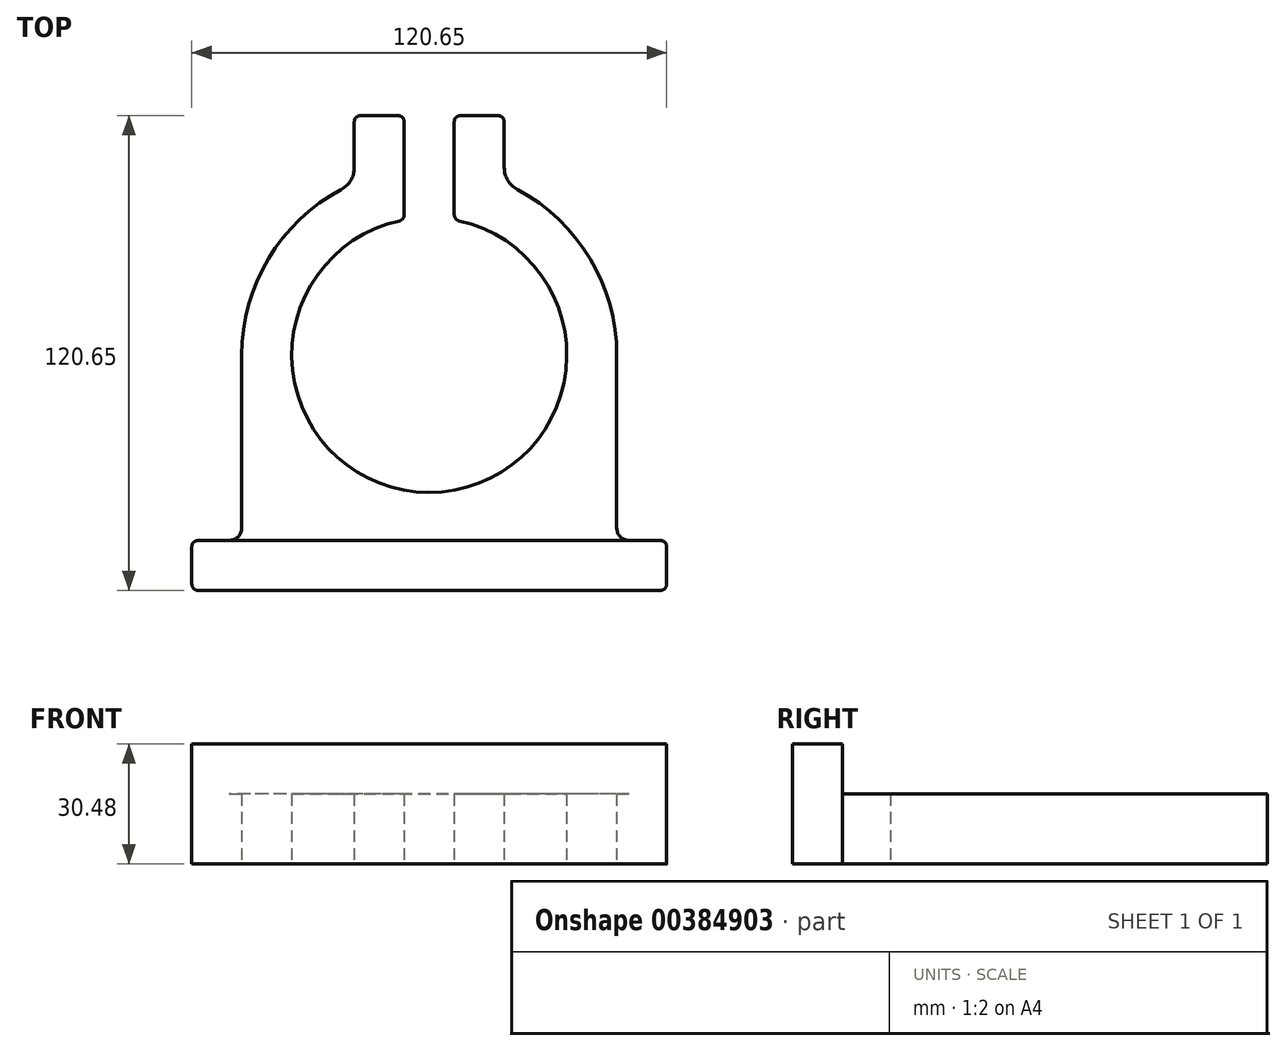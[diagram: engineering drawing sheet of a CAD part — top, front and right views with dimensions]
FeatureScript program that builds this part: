
annotation { "Feature Type Name" : "Feature", "Feature Type Description" : "" }
export const myFeature = defineFeature(function(context is Context, id is Id, definition is map)
    precondition{}
    {
        {
            var Q0;
            Q0=qCreatedBy(makeId("Top.planeOp"),FACE);
            var sketch = newSketch(context, id + "F0", { "sketchPlane" : qUnion([Q0])});
            skLineSegment(sketch, "E0", {"start": v(1.59, 0) * mm, "end": v(119.06, 0) * mm});
            skLineSegment(sketch, "E1", {"start": v(120.65, 1.59) * mm, "end": v(120.65, 11.11) * mm});
            skLineSegment(sketch, "E2", {"start": v(119.06, 12.7) * mm, "end": v(111.13, 12.7) * mm});
            skLineSegment(sketch, "E3", {"start": v(107.95, 15.88) * mm, "end": v(107.95, 59.82) * mm});
            skLineSegment(sketch, "E4", {"start": v(12.7, 59.82) * mm, "end": v(12.7, 15.88) * mm});
            skLineSegment(sketch, "E5", {"start": v(9.52, 12.7) * mm, "end": v(1.59, 12.7) * mm});
            skLineSegment(sketch, "E6", {"start": v(0, 11.11) * mm, "end": v(0, 1.59) * mm});
            skArc(sketch, "E7", {"start": v(107.95, 59.82) * mm, "mid": v(101.16, 84.32) * mm, "end": v(82.74, 101.84) * mm});
            skPoint(sketch, "E7.startSnap0", {"position": v(60.33, 59.82) * mm});
            skLineSegment(sketch, "E8.trimOffspring", {"start": v(107.95, 59.82) * mm, "end": v(107.95, 59.82) * mm});
            skPoint(sketch, "E9.orphan", {"position": v(60.33, 107.44) * mm});
            skArc(sketch, "E10", {"start": v(52.73, 93.9) * mm, "mid": v(60.33, 24.9) * mm, "end": v(67.92, 93.9) * mm});
            skLineSegment(sketch, "E11", {"start": v(53.98, 95.46) * mm, "end": v(53.98, 119.06) * mm});
            skLineSegment(sketch, "E12", {"start": v(52.39, 120.65) * mm, "end": v(42.86, 120.65) * mm});
            skLineSegment(sketch, "E13", {"start": v(41.28, 119.06) * mm, "end": v(41.28, 107.44) * mm});
            skLineSegment(sketch, "E14", {"start": v(60.33, 59.82) * mm, "end": v(60.33, 128.19) * mm, "construction": true});
            skLineSegment(sketch, "E15.MirrorCS", {"start": v(66.67, 95.46) * mm, "end": v(66.67, 119.06) * mm});
            skLineSegment(sketch, "E16.MirrorCS", {"start": v(68.26, 120.65) * mm, "end": v(77.79, 120.65) * mm});
            skLineSegment(sketch, "E17.MirrorCS", {"start": v(79.38, 119.06) * mm, "end": v(79.38, 107.44) * mm});
            skArc(sketch, "E18.trimOffspring", {"start": v(37.91, 101.84) * mm, "mid": v(19.49, 84.32) * mm, "end": v(12.7, 59.82) * mm});
            skLineSegment(sketch, "E19", {"start": v(60.33, 0) * mm, "end": v(60.33, 37.1) * mm, "construction": true});
            skPoint(sketch, "E20.visualSharp", {"position": v(41.28, 103.47) * mm});
            skArc(sketch, "E20.filletArc", {"start": v(37.91, 101.84) * mm, "mid": v(40.37, 104.17) * mm, "end": v(41.28, 107.44) * mm});
            skPoint(sketch, "E21.visualSharp", {"position": v(79.38, 103.47) * mm});
            skArc(sketch, "E21.filletArc", {"start": v(79.38, 107.44) * mm, "mid": v(80.28, 104.17) * mm, "end": v(82.74, 101.84) * mm});
            skPoint(sketch, "E22.visualSharp", {"position": v(107.95, 12.7) * mm});
            skPoint(sketch, "E23.visualSharp", {"position": v(12.7, 12.7) * mm});
            skArc(sketch, "E24.filletArc", {"start": v(52.73, 93.9) * mm, "mid": v(53.63, 94.46) * mm, "end": v(53.98, 95.46) * mm});
            skPoint(sketch, "E25.visualSharp", {"position": v(120.65, 12.7) * mm});
            skArc(sketch, "E25.filletArc", {"start": v(120.65, 11.11) * mm, "mid": v(120.19, 12.24) * mm, "end": v(119.06, 12.7) * mm});
            skPoint(sketch, "E26.visualSharp", {"position": v(120.65, 0) * mm});
            skArc(sketch, "E26.filletArc", {"start": v(119.06, 0) * mm, "mid": v(120.19, 0.46) * mm, "end": v(120.65, 1.59) * mm});
            skPoint(sketch, "E27.visualSharp", {"position": v(0, 0) * mm});
            skArc(sketch, "E27.filletArc", {"start": v(0, 1.59) * mm, "mid": v(0.46, 0.46) * mm, "end": v(1.59, 0) * mm});
            skPoint(sketch, "E28.visualSharp", {"position": v(0, 12.7) * mm});
            skArc(sketch, "E28.filletArc", {"start": v(1.59, 12.7) * mm, "mid": v(0.46, 12.24) * mm, "end": v(0, 11.11) * mm});
            skPoint(sketch, "E29.visualSharp", {"position": v(66.67, 94.16) * mm});
            skArc(sketch, "E29.filletArc", {"start": v(66.67, 95.46) * mm, "mid": v(67.02, 94.46) * mm, "end": v(67.92, 93.9) * mm});
            skPoint(sketch, "E30.visualSharp", {"position": v(41.28, 120.65) * mm});
            skArc(sketch, "E30.filletArc", {"start": v(42.86, 120.65) * mm, "mid": v(41.74, 120.19) * mm, "end": v(41.28, 119.06) * mm});
            skPoint(sketch, "E31.visualSharp", {"position": v(53.98, 120.65) * mm});
            skArc(sketch, "E31.filletArc", {"start": v(53.98, 119.06) * mm, "mid": v(53.51, 120.19) * mm, "end": v(52.39, 120.65) * mm});
            skPoint(sketch, "E32.visualSharp", {"position": v(79.38, 120.65) * mm});
            skArc(sketch, "E32.filletArc", {"start": v(79.38, 119.06) * mm, "mid": v(78.91, 120.19) * mm, "end": v(77.79, 120.65) * mm});
            skPoint(sketch, "E33.visualSharp", {"position": v(66.67, 120.65) * mm});
            skArc(sketch, "E33.filletArc", {"start": v(68.26, 120.65) * mm, "mid": v(67.14, 120.19) * mm, "end": v(66.67, 119.06) * mm});
            skArc(sketch, "E34.filletArc", {"start": v(9.52, 12.7) * mm, "mid": v(11.77, 13.63) * mm, "end": v(12.7, 15.88) * mm});
            skArc(sketch, "E35.filletArc", {"start": v(107.95, 15.88) * mm, "mid": v(108.88, 13.63) * mm, "end": v(111.13, 12.7) * mm});
            skSolve(sketch);
        }
        {
            var Q0;
            Q0 = qSketchRegion(id + "F0", true);
            extrude(context, id + "F1", {"entities" : qUnion([Q0]), "depth" : 30.48 * mm});
        }
        {
            var Q0;
            Q0=makeQuery(id+"F1.opExtrude","CAP_FACE",FACE,{"disambiguationData":[OSD([sQuery(id+"F0.wireOp",EDGE,"E0"),sQuery(id+"F0.wireOp",EDGE,"E1"),sQuery(id+"F0.wireOp",EDGE,"E2"),sQuery(id+"F0.wireOp",EDGE,"E3"),sQuery(id+"F0.wireOp",EDGE,"E4"),sQuery(id+"F0.wireOp",EDGE,"E5"),sQuery(id+"F0.wireOp",EDGE,"E6"),sQuery(id+"F0.wireOp",EDGE,"E7"),sQuery(id+"F0.wireOp",EDGE,"E10"),sQuery(id+"F0.wireOp",EDGE,"E11"),sQuery(id+"F0.wireOp",EDGE,"E12"),sQuery(id+"F0.wireOp",EDGE,"E13"),sQuery(id+"F0.wireOp",EDGE,"E15.MirrorCS"),sQuery(id+"F0.wireOp",EDGE,"E16.MirrorCS"),sQuery(id+"F0.wireOp",EDGE,"E17.MirrorCS"),sQuery(id+"F0.wireOp",EDGE,"E18.trimOffspring"),sQuery(id+"F0.wireOp",EDGE,"E20.filletArc"),sQuery(id+"F0.wireOp",EDGE,"E21.filletArc"),sQuery(id+"F0.wireOp",EDGE,"E22.filletArc"),sQuery(id+"F0.wireOp",EDGE,"E23.filletArc"),sQuery(id+"F0.wireOp",EDGE,"E24.filletArc"),sQuery(id+"F0.wireOp",EDGE,"E25.filletArc"),sQuery(id+"F0.wireOp",EDGE,"E26.filletArc"),sQuery(id+"F0.wireOp",EDGE,"E27.filletArc"),sQuery(id+"F0.wireOp",EDGE,"E28.filletArc"),sQuery(id+"F0.wireOp",EDGE,"E29.filletArc"),sQuery(id+"F0.wireOp",EDGE,"E30.filletArc"),sQuery(id+"F0.wireOp",EDGE,"E31.filletArc"),sQuery(id+"F0.wireOp",EDGE,"E32.filletArc"),sQuery(id+"F0.wireOp",EDGE,"E33.filletArc")])],"isStart":false});
            var sketch = newSketch(context, id + "F2", { "sketchPlane" : qUnion([Q0])});
            skPoint(sketch, "E36.oppositeSnap0", {"position": v(66.67, 107.26) * mm});
            skArc(sketch, "E37.converted", {"start": v(119.06, 32.23) * mm, "mid": v(60.32, 156.97) * mm, "end": v(1.59, 32.23) * mm});
            skLineSegment(sketch, "E38", {"start": v(1.59, 12.7) * mm, "end": v(119.06, 12.7) * mm});
            skLineSegment(sketch, "E39", {"start": v(1.59, 12.7) * mm, "end": v(1.59, 32.23) * mm});
            skLineSegment(sketch, "E40", {"start": v(119.06, 12.7) * mm, "end": v(119.06, 32.23) * mm});
            skSolve(sketch);
        }
        {
            var Q0;
            Q0 = qSketchRegion(id + "F2", true);
            extrude(context, id + "F3", {"entities" : qUnion([Q0]), "operationType" : NewBodyOperationType.REMOVE, "oppositeDirection" : true, "depth" : 12.7 * mm});
        }
    });
